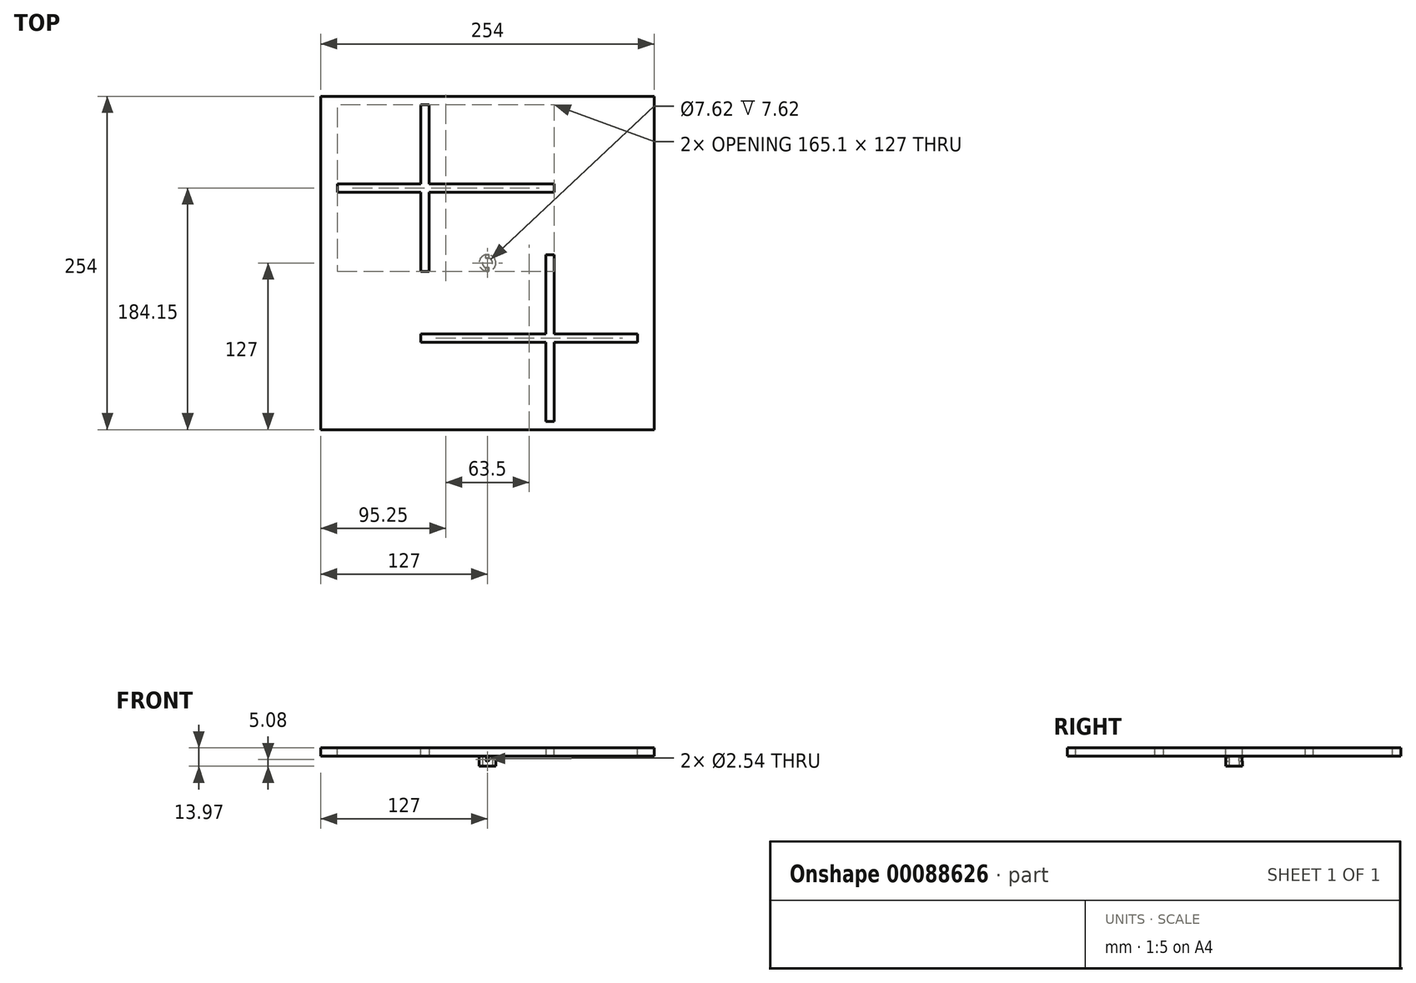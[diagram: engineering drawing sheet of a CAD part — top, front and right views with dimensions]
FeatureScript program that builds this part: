
annotation { "Feature Type Name" : "Feature", "Feature Type Description" : "" }
export const myFeature = defineFeature(function(context is Context, id is Id, definition is map)
    precondition{}
    {
        {
            var Q0;
            Q0=qCreatedBy(makeId("Top.planeOp"),FACE);
            var sketch = newSketch(context, id + "F0", { "sketchPlane" : qUnion([Q0])});
            skLineSegment(sketch, "E0.bottom", {"start": v(127, -127) * mm, "end": v(-127, -127) * mm});
            skLineSegment(sketch, "E0.top", {"start": v(127, 127) * mm, "end": v(-127, 127) * mm});
            skLineSegment(sketch, "E0.left", {"start": v(127, -127) * mm, "end": v(127, 127) * mm});
            skLineSegment(sketch, "E0.right", {"start": v(-127, -127) * mm, "end": v(-127, 127) * mm});
            skPoint(sketch, "E0.middle", {"position": v(0, 0) * mm});
            skSolve(sketch);
        }
        {
            var Q0;
            Q0 = qSketchRegion(id + "F0", true);
            extrude(context, id + "F1", {"entities" : qUnion([Q0]), "depth" : 6.35 * mm});
        }
        {
            var Q0;
            Q0=makeQuery(id+"F1.opExtrude","CAP_FACE",FACE,{"disambiguationData":[OSD([sQuery(id+"F0.wireOp",EDGE,"E0.bottom"),sQuery(id+"F0.wireOp",EDGE,"E0.top"),sQuery(id+"F0.wireOp",EDGE,"E0.left"),sQuery(id+"F0.wireOp",EDGE,"E0.right")])],"isStart":false});
            var sketch = newSketch(context, id + "F2", { "sketchPlane" : qUnion([Q0])});
            skLineSegment(sketch, "E1.bottom", {"start": v(-50.8, 120.65) * mm, "end": v(-44.45, 120.65) * mm});
            skLineSegment(sketch, "E1.top", {"start": v(-50.8, -6.35) * mm, "end": v(-44.45, -6.35) * mm});
            skLineSegment(sketch, "E1.left", {"start": v(-50.8, 120.65) * mm, "end": v(-50.8, -6.35) * mm});
            skLineSegment(sketch, "E1.right", {"start": v(-44.45, 120.65) * mm, "end": v(-44.45, -6.35) * mm});
            skSolve(sketch);
        }
        {
            var Q0;
            Q0=makeQuery(id+"F1.opExtrude","CAP_FACE",FACE,{"disambiguationData":[OSD([sQuery(id+"F0.wireOp",EDGE,"E0.bottom"),sQuery(id+"F0.wireOp",EDGE,"E0.top"),sQuery(id+"F0.wireOp",EDGE,"E0.left"),sQuery(id+"F0.wireOp",EDGE,"E0.right")])],"isStart":false});
            var sketch = newSketch(context, id + "F3", { "sketchPlane" : qUnion([Q0])});
            skLineSegment(sketch, "E2.bottom", {"start": v(-50.8, -53.98) * mm, "end": v(114.3, -53.97) * mm});
            skLineSegment(sketch, "E2.top", {"start": v(-50.8, -60.33) * mm, "end": v(114.3, -60.32) * mm});
            skLineSegment(sketch, "E2.left", {"start": v(-50.8, -53.98) * mm, "end": v(-50.8, -60.33) * mm});
            skLineSegment(sketch, "E2.right", {"start": v(114.3, -53.97) * mm, "end": v(114.3, -60.32) * mm});
            skLineSegment(sketch, "E3.left", {"start": v(114.3, -57.15) * mm, "end": v(114.3, -56.92) * mm});
            skLineSegment(sketch, "E3.right", {"start": v(127, -0.23) * mm, "end": v(127, 0) * mm});
            skSolve(sketch);
        }
        {
            var Q0;
            Q0 = qSketchRegion(id + "F3", true);
            extrude(context, id + "F4", {"entities" : qUnion([Q0]), "operationType" : NewBodyOperationType.REMOVE, "oppositeDirection" : true, "depth" : 25.4 * mm});
        }
        {
            var Q0;
            Q0=makeQuery(id+"F1.opExtrude","CAP_FACE",FACE,{"disambiguationData":[OSD([sQuery(id+"F0.wireOp",EDGE,"E0.bottom"),sQuery(id+"F0.wireOp",EDGE,"E0.top"),sQuery(id+"F0.wireOp",EDGE,"E0.left"),sQuery(id+"F0.wireOp",EDGE,"E0.right")])],"isStart":false});
            var sketch = newSketch(context, id + "F5", { "sketchPlane" : qUnion([Q0])});
            skLineSegment(sketch, "E4.bottom", {"start": v(44.45, 6.35) * mm, "end": v(50.8, 6.35) * mm});
            skLineSegment(sketch, "E4.top", {"start": v(44.45, -120.65) * mm, "end": v(50.8, -120.65) * mm});
            skLineSegment(sketch, "E4.left", {"start": v(44.45, 6.35) * mm, "end": v(44.45, -120.65) * mm});
            skLineSegment(sketch, "E4.right", {"start": v(50.8, 6.35) * mm, "end": v(50.8, -120.65) * mm});
            skSolve(sketch);
        }
        {
            var Q0;
            Q0 = qSketchRegion(id + "F5", true);
            extrude(context, id + "F6", {"entities" : qUnion([Q0]), "operationType" : NewBodyOperationType.REMOVE, "oppositeDirection" : true, "depth" : 25.4 * mm});
        }
        {
            var Q0;
            Q0=makeQuery(id+"F1.opExtrude","CAP_FACE",FACE,{"disambiguationData":[OSD([sQuery(id+"F0.wireOp",EDGE,"E0.bottom"),sQuery(id+"F0.wireOp",EDGE,"E0.top"),sQuery(id+"F0.wireOp",EDGE,"E0.left"),sQuery(id+"F0.wireOp",EDGE,"E0.right")])],"isStart":false});
            var sketch = newSketch(context, id + "F7", { "sketchPlane" : qUnion([Q0])});
            skLineSegment(sketch, "E5.bottom", {"start": v(-114.3, 60.32) * mm, "end": v(50.8, 60.32) * mm});
            skLineSegment(sketch, "E5.top", {"start": v(-114.3, 53.97) * mm, "end": v(50.8, 53.97) * mm});
            skLineSegment(sketch, "E5.left", {"start": v(-114.3, 60.32) * mm, "end": v(-114.3, 53.97) * mm});
            skLineSegment(sketch, "E5.right", {"start": v(50.8, 60.32) * mm, "end": v(50.8, 53.97) * mm});
            skSolve(sketch);
        }
        {
            var Q0;
            Q0 = qSketchRegion(id + "F7", true);
            extrude(context, id + "F8", {"entities" : qUnion([Q0]), "operationType" : NewBodyOperationType.REMOVE, "oppositeDirection" : true, "depth" : 25.4 * mm});
        }
        {
            var Q0;
            Q0=makeQuery(id+"F1.opExtrude","CAP_FACE",FACE,{"disambiguationData":[OSD([sQuery(id+"F0.wireOp",EDGE,"E0.bottom"),sQuery(id+"F0.wireOp",EDGE,"E0.top"),sQuery(id+"F0.wireOp",EDGE,"E0.left"),sQuery(id+"F0.wireOp",EDGE,"E0.right")])],"isStart":true});
            var sketch = newSketch(context, id + "F9", { "sketchPlane" : qUnion([Q0])});
            skCircle(sketch, "E6", {"center": v(0, 0) * mm, "radius": 6.35 * mm});
            skSolve(sketch);
        }
        {
            var Q0;
            Q0 = qSketchRegion(id + "F9", true);
            extrude(context, id + "F10", {"entities" : qUnion([Q0]), "operationType" : NewBodyOperationType.ADD, "depth" : 7.62 * mm});
        }
        {
            var Q0;
            Q0=makeQuery(id+"F10.opExtrude","CAP_FACE",FACE,{"disambiguationData":[OSD([sQuery(id+"F9.wireOp",EDGE,"E6")])],"isStart":false});
            var sketch = newSketch(context, id + "F11", { "sketchPlane" : qUnion([Q0])});
            skCircle(sketch, "E7", {"center": v(0, 0) * mm, "radius": 3.8 * mm});
            skSolve(sketch);
        }
        {
            var Q0;
            Q0=qCreatedBy(makeId("Front.planeOp"),FACE);
            cPlane(context, id + "F12", {"entities" : qUnion([Q0]), "cplaneType" : CPlaneType.OFFSET, "offset" : 12.7 * mm, "oppositeDirection" : true, "width" : 152.4 * mm, "height" : 152.4 * mm});
        }
        {
            var Q0;
            Q0=qCreatedBy(id+"F12.planeOp",FACE);
            var sketch = newSketch(context, id + "F13", { "sketchPlane" : qUnion([Q0])});
            skCircle(sketch, "E8", {"center": v(0, -2.54) * mm, "radius": 1.27 * mm});
            skSolve(sketch);
        }
        {
            var Q0;
            Q0 = qSketchRegion(id + "F11", true);
            extrude(context, id + "F14", {"entities" : qUnion([Q0]), "operationType" : NewBodyOperationType.REMOVE, "oppositeDirection" : true, "depth" : 7.62 * mm});
        }
        {
            var Q0;
            Q0 = qSketchRegion(id + "F13", true);
            extrude(context, id + "F15", {"entities" : qUnion([Q0]), "operationType" : NewBodyOperationType.REMOVE, "depth" : 25.4 * mm});
        }
        {
            var Q0;
            Q0 = qSketchRegion(id + "F2", true);
            extrude(context, id + "F16", {"entities" : qUnion([Q0]), "operationType" : NewBodyOperationType.REMOVE, "oppositeDirection" : true, "depth" : 25.4 * mm});
        }
    });
